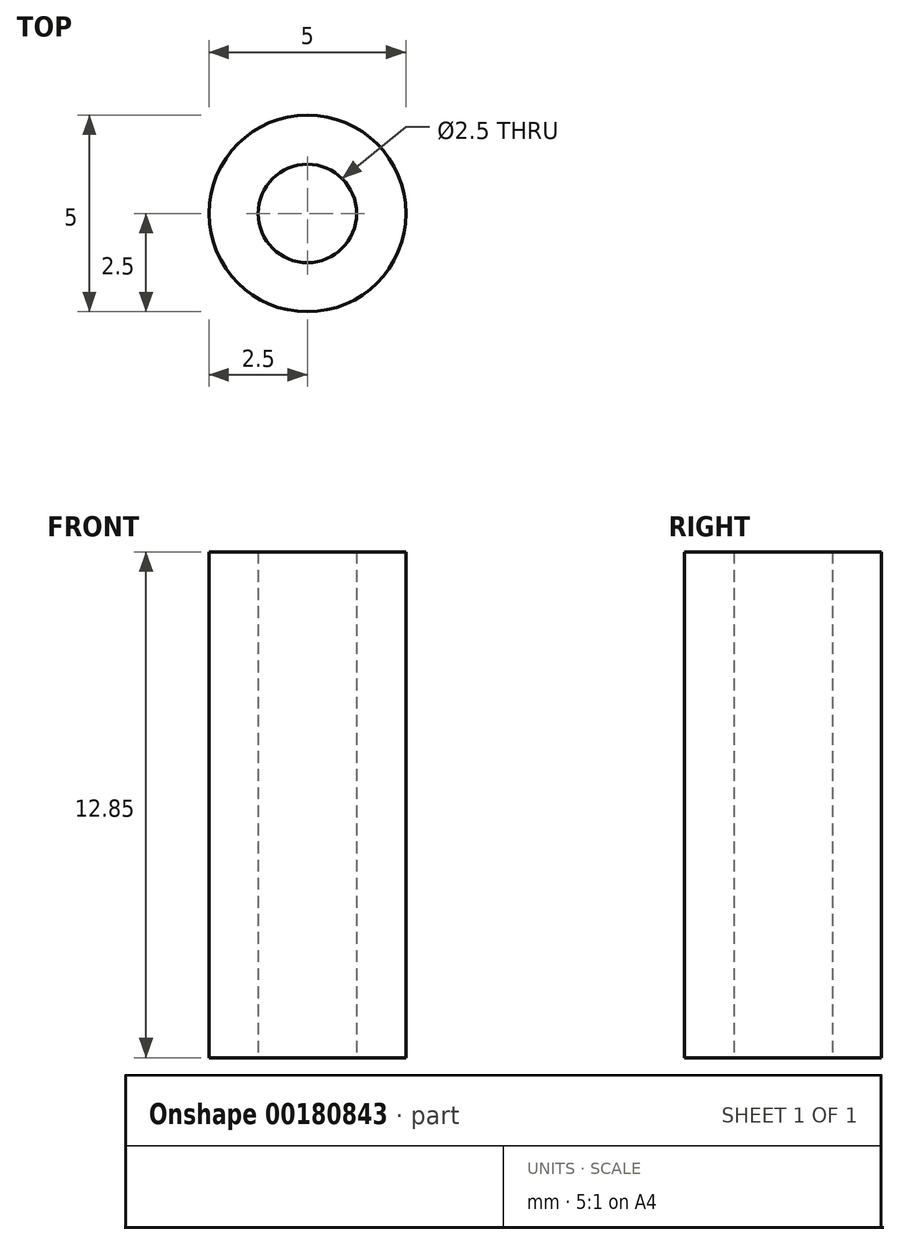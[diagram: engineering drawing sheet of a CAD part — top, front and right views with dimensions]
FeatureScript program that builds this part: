
annotation { "Feature Type Name" : "Feature", "Feature Type Description" : "" }
export const myFeature = defineFeature(function(context is Context, id is Id, definition is map)
    precondition{}
    {
        {
            var Q0;
            Q0=qCreatedBy(makeId("Top.planeOp"),FACE);
            var sketch = newSketch(context, id + "F0", { "sketchPlane" : qUnion([Q0])});
            skCircle(sketch, "E0", {"center": v(0, 0) * mm, "radius": 2.5 * mm});
            skCircle(sketch, "E1", {"center": v(0, 0) * mm, "radius": 1.25 * mm});
            skSolve(sketch);
        }
        {
            var Q0;
            Q0=makeQuery(id+"F0.imprint","IMPRINT",FACE,{"disambiguationData":[TD([[makeQuery(id+"F0.imprint","IMPRINT",EDGE,{"derivedFrom":sQuery(id+"F0.wireOp",EDGE,"E0")}),1.0]])]});
            extrude(context, id + "F1", {"entities" : qUnion([Q0]), "depth" : 12.85 * mm});
        }
    });
